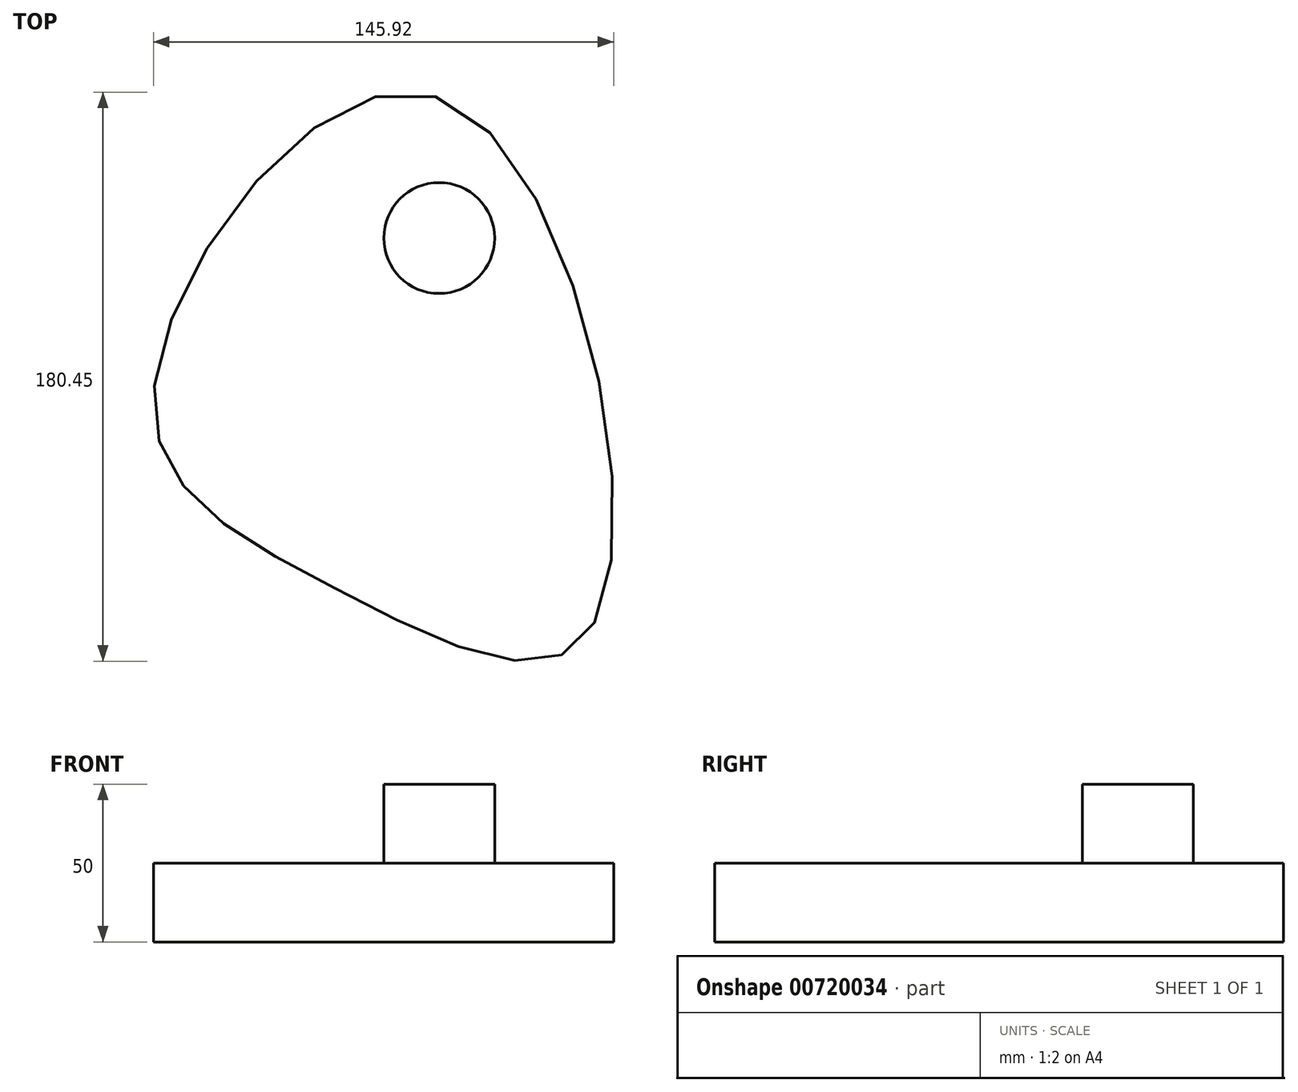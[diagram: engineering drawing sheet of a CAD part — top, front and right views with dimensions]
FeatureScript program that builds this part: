
annotation { "Feature Type Name" : "Feature", "Feature Type Description" : "" }
export const myFeature = defineFeature(function(context is Context, id is Id, definition is map)
    precondition{}
    {
        {
            var Q0;
            Q0=qCreatedBy(makeId("Top.planeOp"),FACE);
            var sketch = newSketch(context, id + "F0", { "sketchPlane" : qUnion([Q0])});
            skFitSpline(sketch, "E0", {"points": [v(-22.65, -28.78) * mm, v(-79.92, 34.42) * mm, v(10.08, 126.91) * mm, v(58.72, -41.6) * mm, v(-22.65, -28.78) * mm]});
            skSolve(sketch);
        }
        {
            var Q0;
            Q0=makeQuery(id+"F0.imprint","IMPRINT",FACE,{"disambiguationData":[TD([[makeQuery(id+"F0.imprint","IMPRINT",EDGE,{"derivedFrom":sQuery(id+"F0.wireOp",EDGE,"E0")}),-1.0]])]});
            extrude(context, id + "F1", {"entities" : qUnion([Q0]), "depth" : 25 * mm, "offsetDistance" : 25 * mm});
        }
        {
            var Q0;
            Q0=makeQuery(id+"F1.opExtrude","CAP_FACE",FACE,{"disambiguationData":[OSD([sQuery(id+"F0.wireOp",EDGE,"E0")])],"isStart":false});
            var sketch = newSketch(context, id + "F2", { "sketchPlane" : qUnion([Q0])});
            skCircle(sketch, "E1", {"center": v(10.53, 82.24) * mm, "radius": 17.57 * mm});
            skSolve(sketch);
        }
        {
            var Q0;
            Q0=makeQuery(id+"F2.imprint","IMPRINT",FACE,{"disambiguationData":[TD([[makeQuery(id+"F2.imprint","IMPRINT",EDGE,{"derivedFrom":sQuery(id+"F2.wireOp",EDGE,"E1")}),1.0]])]});
            extrude(context, id + "F3", {"entities" : qUnion([Q0]), "operationType" : NewBodyOperationType.ADD, "depth" : 25 * mm, "offsetDistance" : 25 * mm});
        }
    });
